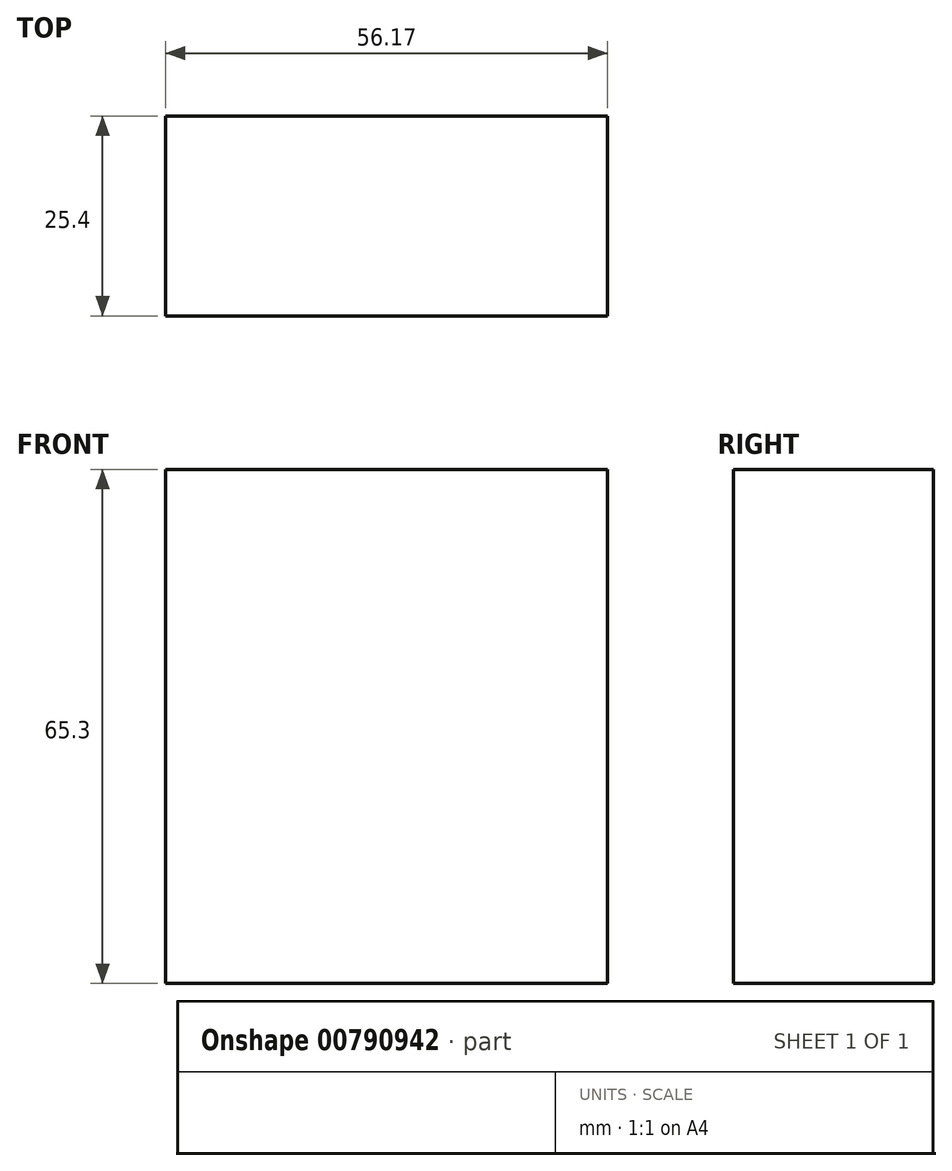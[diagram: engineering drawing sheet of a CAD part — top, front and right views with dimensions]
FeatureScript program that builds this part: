
annotation { "Feature Type Name" : "Feature", "Feature Type Description" : "" }
export const myFeature = defineFeature(function(context is Context, id is Id, definition is map)
    precondition{}
    {
        {
            var Q0;
            Q0=qCreatedBy(makeId("Front.planeOp"),FACE);
            var sketch = newSketch(context, id + "F0", { "sketchPlane" : qUnion([Q0])});
            skLineSegment(sketch, "E0.bottom", {"start": v(0, 65.3) * mm, "end": v(56.17, 65.3) * mm});
            skLineSegment(sketch, "E0.top", {"start": v(0, 0) * mm, "end": v(56.17, 0) * mm});
            skLineSegment(sketch, "E0.left", {"start": v(0, 65.3) * mm, "end": v(0, 0) * mm});
            skLineSegment(sketch, "E0.right", {"start": v(56.17, 65.3) * mm, "end": v(56.17, 0) * mm});
            skSolve(sketch);
        }
        {
            var Q0;
            Q0 = qSketchRegion(id + "F0", true);
            extrude(context, id + "F1", {"entities" : qUnion([Q0]), "depth" : 25.4 * mm, "offsetDistance" : 25.4 * mm});
        }
    });
